# Revit family: Grohe_BottleTrap_29509KF0
name_source: partatom
category: Plumbing Fixtures
units: mm (PartAtom-declared; Revit-internal decimal feet)

## family parameters
Cut with Voids When Loaded = No
Host = Face
OmniClass Number = 23.45.05.00
OmniClass Title = Sanitary Equipment
Part Type = Normal
Room Calculation Point = No
Round Connector Dimension = Use Diameter
Shared = No

## types (1)
- Bottle trap, 1 1/4" (29509KF0)
    Assembly Code = D2010
    AssetType = Fixed
    BIMObjectName = Grohe_BottleTrap_29509KF0
    CO2NeutralProduction = GROHE is one of the first leading manufacturer within the sanitary industry having a CO2-neutral production.
    CW Connection = No
    ClassificationName = Uniclass2015
    ClassificationValue = Pr_65_52_25_75
    Color = Matt Black
    Cost = 0 $
    Default Elevation = 0 mm  [stored 0 ft]
    Description = Bottle trap, 1 1/4"
    DimensionsDocumentLink = https://cdn.cloud.grohe.com
    DocumentationCertificates = https://www.bimstore.co
    DocumentationInstallationGuide = https://www.bimstore.co
    DocumentationLiterature = https://www.bimstore.co
    DocumentationMaintenance = https://www.bimstore.co
    DocumentationTechnical = https://www.bimstore.co
    DurationUnit = Years
    EF000007 = Black
    EF000051 = Cup siphon
    EF000139 = Lacquered
    EF002169 = Brass
    EF011596 = Water / fluid
    EF011610 = 90°-Bend
    EF011611 = FALSE
    EF021480 = TRUE
    EF021487 = TRUE
    EF021703 = 32
    EF021707 = FALSE
    EF021710 = Slide end
    EF021711 = Union nut
    EF021713 = FALSE
    EF021714 = FALSE
    EF021715 = FALSE
    EF021716 = FALSE
    EF021719 = FALSE
    EF021720 = FALSE
    EF021847 = 1 1/4 inch (32)
    EF022330 = Side
    EF025109 = Other
    EFSE0002 = FALSE
    Ecojoy = No
    ExpectedLife = 0
    FullRecyclabilityOfPlastic = All plastic components are fully recyclable
    GROHESocialCommittment = green.grohe.com/social_engagement
    GROHESustainability = green.grohe.com
    HW Connection = No
    IfcExportAs = IfcPipeFitting
    IfcExportType = IfcPipeFittingType
    Keynote = N13
    Manufacturer = Grohe
    ManufacturerName = Grohe
    Model = Bottle trap, 1 1/4"
    ModelNumber = 29509KF0
    ModelReference = Bottle trap, 1 1/4"
    NBSDescription = Sanitary appliance traps
    NBSObjectName = Grohe - Sanitary appliance traps
    NBSReference = 90-10-60/410
    NominalDepth = 0 mm  [stored 0 ft]
    NominalHeight = 0 mm  [stored 0 ft]
    NominalLength = 0 mm  [stored 0 ft]
    OffsetMax = 287 mm  [stored 0.941601 ft]
    OffsetMin = 132 mm  [stored 0.433071 ft]
    PrimaryMaterial = Grohe_MattBlack
    ProductDescription = for basins

brass

(screw-top for cleaning)

large sliding escutcheon

GROHE Long-Life Shine finish
    ProductNumber = 29509KF0
    ProductPageURL = https://www.grohe.co.uk
    ProductShortText = Bottle trap, 1 1/4"
    ProductType = Inlet-, Waste- +Overflow Fitti
    ProductionYear = 2023
    SustainabilityAward = green.grohe.com/awards
    SustainabilityReport = green.grohe.com/reporting
    TPIDocumentLink = https://cdn.cloud.grohe.com
    Type Comments = Bottle trap, 1 1/4"
    TypeName = Bottle trap, 1 1/4"
    URL = https://www.grohe.co.uk
    Vent Connection = No
    WarrantyDurationLabor = 0
    WarrantyDurationParts = 0
    WarrantyDurationUnit = Years
    Waste Connection = Yes
    _BSBibleVersion = 17
    _BimSpecGuid = 0
    _CurrentRevision = 1
    _DistributedBy = https://www.bimstore.co
    _ObjectUserGuide = https://www.bimstore.co

note: [stored X ft] marks values corroborated as IEEE doubles in the binary element streams (Revit-internal decimal feet)

## geometry (parser evidence)
native form markers: Sweep x1
no freeform markers — native parametric forms only
